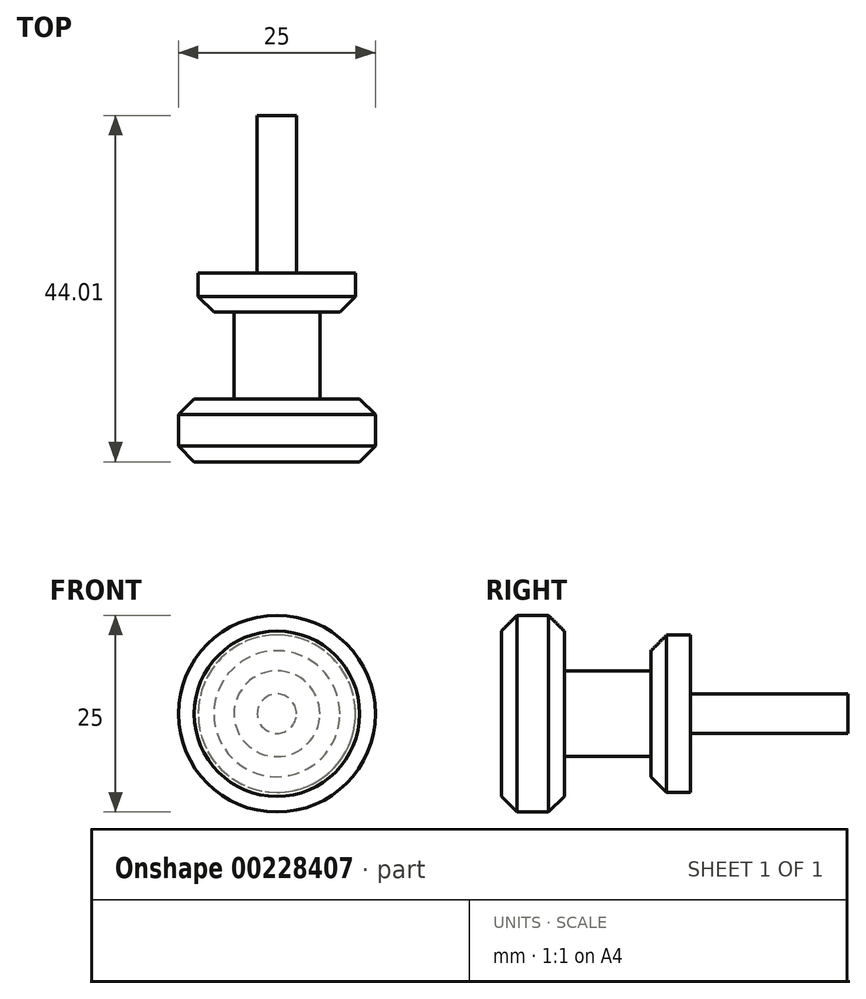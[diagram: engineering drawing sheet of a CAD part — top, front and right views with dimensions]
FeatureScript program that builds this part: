
annotation { "Feature Type Name" : "Feature", "Feature Type Description" : "" }
export const myFeature = defineFeature(function(context is Context, id is Id, definition is map)
    precondition{}
    {
        {
            var Q0;
            Q0=qCreatedBy(makeId("Right.planeOp"),FACE);
            var sketch = newSketch(context, id + "F0", { "sketchPlane" : qUnion([Q0])});
            skLineSegment(sketch, "E0.top", {"start": v(10, 2.5) * mm, "end": v(-10, 2.5) * mm});
            skLineSegment(sketch, "E0.left", {"start": v(10, 0) * mm, "end": v(10, 2.5) * mm});
            skPoint(sketch, "E0.middle", {"position": v(0, 0) * mm});
            skLineSegment(sketch, "E1.bottom", {"start": v(-10, 10) * mm, "end": v(-15, 10) * mm});
            skLineSegment(sketch, "E1.left", {"start": v(-10, 10) * mm, "end": v(-10, 2.5) * mm});
            skLineSegment(sketch, "E1.right", {"start": v(-15, 10) * mm, "end": v(-15, 5.45) * mm});
            skPoint(sketch, "E1.middle", {"position": v(-12.5, 0) * mm});
            skLineSegment(sketch, "E2.bottom", {"start": v(-15, 5.45) * mm, "end": v(-26, 5.45) * mm});
            skPoint(sketch, "E2.middle", {"position": v(-20.5, 0) * mm});
            skLineSegment(sketch, "E3.bottom", {"start": v(-26, 12.5) * mm, "end": v(-34, 12.5) * mm});
            skLineSegment(sketch, "E3.left", {"start": v(-26, 12.5) * mm, "end": v(-26, 5.45) * mm});
            skLineSegment(sketch, "E3.right", {"start": v(-34, 12.5) * mm, "end": v(-34, 0) * mm});
            skPoint(sketch, "E3.middle", {"position": v(-30, 0) * mm});
            skPoint(sketch, "E3.cornerSnap0", {"position": v(-26, 0) * mm});
            skLineSegment(sketch, "E4", {"start": v(-46.24, 0) * mm, "end": v(20.74, 0) * mm, "construction": true});
            skPoint(sketch, "E3.top.end.orphan", {"position": v(-34, -12.5) * mm});
            skPoint(sketch, "E5.orphan", {"position": v(-26, -12.5) * mm});
            skPoint(sketch, "E6.orphan", {"position": v(-26, -5.45) * mm});
            skPoint(sketch, "E7.orphan", {"position": v(-15, -5.45) * mm});
            skPoint(sketch, "E1.top.end.orphan", {"position": v(-15, -10) * mm});
            skPoint(sketch, "E8.orphan", {"position": v(-10, -10) * mm});
            skPoint(sketch, "E9.orphan", {"position": v(10, -2.5) * mm});
            skPoint(sketch, "E10.orphan", {"position": v(-10, -2.5) * mm});
            skLineSegment(sketch, "E11", {"start": v(-34, 0) * mm, "end": v(10, 0) * mm});
            skSolve(sketch);
        }
        {
            var Q0;
            Q0 = qSketchRegion(id + "F0", true);
            var Q1;
            Q1=sQuery(id+"F0.wireOp",EDGE,"E4");
            revolve(context, id + "F1", {"entities" : qUnion([Q0]), "axis" : qUnion([Q1]), "revolveType" : RevolveType.FULL});
        }
        {
            var Q0;
            Q0=makeQuery(id+"F1.opRevolve","SWEPT_EDGE",EDGE,{"disambiguationData":[OSD([sQuery(id+"F0.wireOp",EDGE,"E3.bottom"),sQuery(id+"F0.wireOp",EDGE,"E3.right")])]});
            var Q1;
            Q1=makeQuery(id+"F1.opRevolve","SWEPT_EDGE",EDGE,{"disambiguationData":[OSD([sQuery(id+"F0.wireOp",EDGE,"E3.bottom"),sQuery(id+"F0.wireOp",EDGE,"E3.left")])]});
            var Q2;
            Q2=makeQuery(id+"F1.opRevolve","SWEPT_EDGE",EDGE,{"disambiguationData":[OSD([sQuery(id+"F0.wireOp",EDGE,"E1.bottom"),sQuery(id+"F0.wireOp",EDGE,"E1.right")])]});
            chamfer(context, id + "F2", {"entities" : qUnion([Q0, Q1, Q2]), "width" : 2 * mm, "tangentPropagation" : true});
        }
    });
